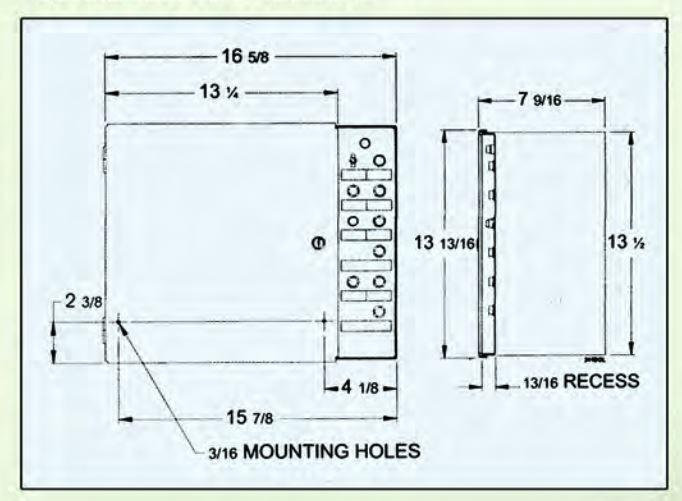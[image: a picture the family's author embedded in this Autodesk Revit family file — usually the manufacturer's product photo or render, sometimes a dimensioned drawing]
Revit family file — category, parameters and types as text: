
# Revit family: Boiler-Weil-McLain-LGB4_12
name_source: partatom
category: Mechanical Equipment
units: mm (PartAtom-declared; Revit-internal decimal feet)

## family parameters
Always vertical = Yes
Cut with Voids When Loaded = No
OmniClass Number = 23.75.10.11.14.11
OmniClass Title = Cast-Iron Boilers
Part Type = Normal
Room Calculation Point = No
Round Connector Dimension = Use Radius
Shared = No
Work Plane-Based = No

## types (1)
- Boiler-Weil-McLain-LGB4_12
    Apparent Load = 0 VA
    Boiler Horsepower = 9.7
    Casing = Metal - Weil-McLain - Paint Grey
    Description = LGB Commercial Gas Boiler
    Draft Hood Outlet = 10"
    Draft Hood Outlet Radius = 5"
    Frequency = 60 Hz
    Gas Connection Radius = 1"
    Gas Connection Size = 1"
    Gas Net IBR = 0.0 Btu/h
    Gross IBR = 0.0 Btu/h
    Height = 4' - 2 3/8"
    Length = 3' - 10 1/2"
    Manufacturer = Weil-McLain
    Model = LGB-4
    Net IBR = 0.0 Btu/h
    Number of Poles = 1
    Optional WFFP Control Panel = No
    Phase = 1
    Power Factor = 1
    Product Documentation Link = http://www.weil-mclain.com
    Product Name = LGB
    Product Page URL = http://www.weil-mclain.com
    Return = 5"
    Return Radius = 3"
    Supply = 6"
    Supply Radius = 3"
    URL = http://www.weil-mclain.com
    Voltage = 120 V
    Width = 1' - 9"

## geometry (parser evidence)
native form markers: Blend x12, Sweep x7
no freeform markers — native parametric forms only
